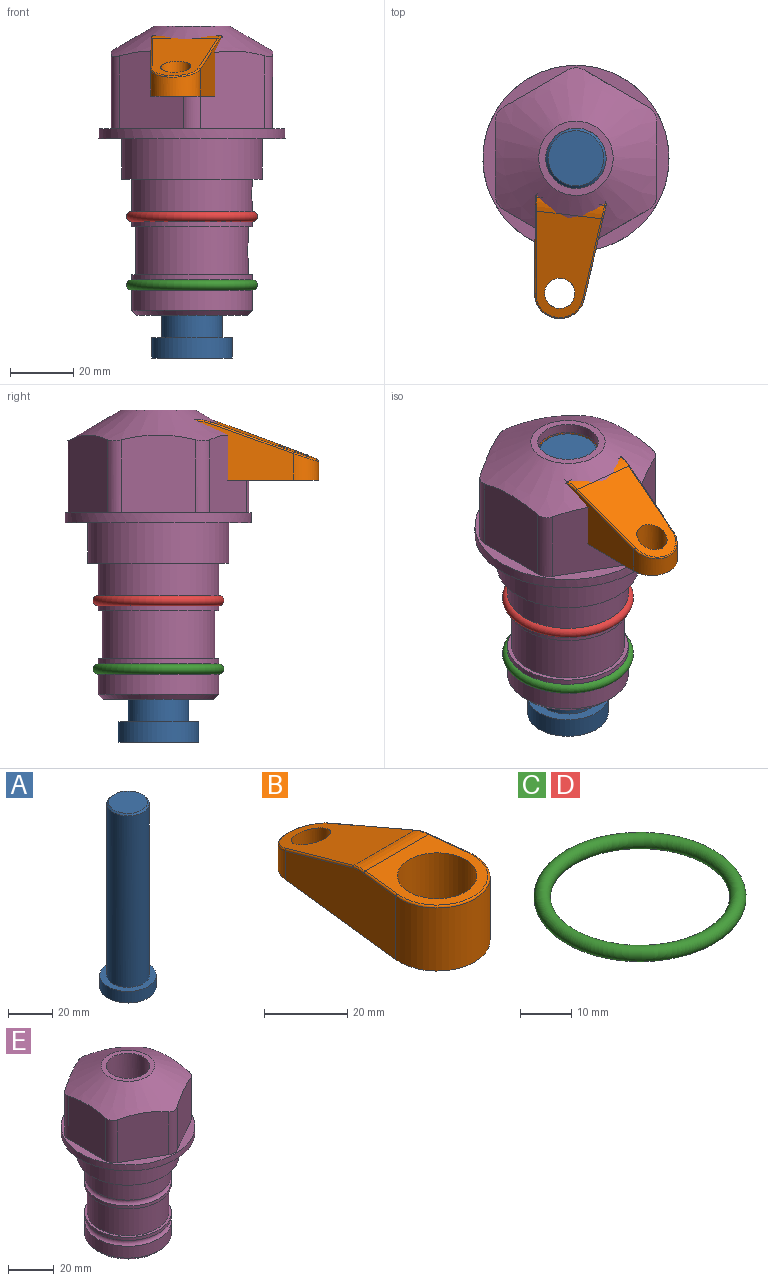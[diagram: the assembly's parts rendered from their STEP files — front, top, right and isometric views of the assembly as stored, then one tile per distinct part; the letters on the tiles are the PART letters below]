
ASSEMBLY  parts=5 mates=3
PART A: 6 faces, bbox 25.4x25.4x101.6 mm
  f0: plane 17.46x17.46mm, normal (0,0,1), area 239.5mm2, adj f5
  f1: plane 25.4x25.4mm, normal (0,0,-1), area 506.7mm2, adj f2
  f2: cylinder r=12.7mm len=25.4mm, axis (0,0,1), area 506.7mm2, adj f1,f3
  f3: plane 25.4x25.4mm, normal (0,0,1), area 221.7mm2, adj f2,f4
  f4: cylinder r=9.53mm len=94.46mm, axis (0,0,1), area 5653mm2, adj f3,f5
  f5: cone r=8.73mm half-angle=45deg, axis (0,0,-1), area 64.4mm2, adj f0,f4
PART B: 44 faces, bbox 27.5x64.5x19.1 mm
  f0: plane 2.3x0.95mm, normal (0,0,-1), area 1mm2, adj f25,f30,f34
  f1: plane 63.5x25.4mm, normal (0,0,-1), area 561.7mm2, adj f2,f3,f4,f5,f6,f7,f19,f20
  f2: cylinder r=12.7mm len=25.4mm, axis (0,0,-1), area 792.2mm2, adj f1,f3,f5,f13
  f3: plane 42.33x18.54mm, normal (0.99,0.11,0), area 647mm2, adj f1,f2,f4,f11,f12,f14
  f4: cylinder r=7.94mm len=15.78mm, axis (0,0,-1), area 158.6mm2, adj f1,f3,f5,f16
  f5: plane 42.33x18.54mm, normal (-0.99,0.11,0), area 647mm2, adj f1,f2,f4,f15,f17,f18
  f6: cylinder r=9.53mm len=19.05mm, axis (0,0,-1), area 1140.1mm2, adj f1,f8
  f7: cylinder r=4.76mm len=10.98mm, axis (0,0,-1), area 276.1mm2, adj f1,f9
  f8: plane 25.83x24.38mm, normal (0,0,1), area 262.2mm2, adj f6,f10,f11,f13,f15
  f9: plane 32.49x20.55mm, normal (0,0.34,0.94), area 489.9mm2, adj f7,f10,f14,f16,f18
  f10: cylinder r=12.7mm len=21.49mm, axis (-1,0,0), area 93.2mm2, adj f8,f9,f12,f17
  f11: cylinder r=0.51mm len=12.34mm, axis (0.11,-0.99,0), area 9.9mm2, adj f3,f8,f12,f13
  f12: bspline ~7.62x1.64mm, area 3.5mm2, adj f3,f10,f11,f14
  f13: torus R=12.19mm, axis (0,0,1), area 33.6mm2, adj f2,f8,f11,f15
  f14: cylinder r=0.51mm len=26.01mm, axis (0.1,-0.93,0.34), area 21.6mm2, adj f3,f9,f12,f16
  f15: cylinder r=0.51mm len=12.34mm, axis (0.11,0.99,0), area 9.9mm2, adj f5,f8,f13,f17
  f16: bspline ~15.78x7.05mm, area 15.7mm2, adj f4,f9,f14,f18
  f17: bspline ~7.62x1.64mm, area 3.5mm2, adj f5,f10,f15,f18
  f18: cylinder r=0.51mm len=26.01mm, axis (0.1,0.93,-0.34), area 21.6mm2, adj f5,f9,f16,f17
  f19: plane 21.6x14.29mm, normal (-0.99,-0.11,0), area 242.6mm2, adj f1,f26,f28,f34,f36,f38
  f20: plane 21.6x14.29mm, normal (0.99,-0.11,0), area 242.6mm2, adj f1,f27,f29,f37,f39,f41
  f21: cylinder r=12.7mm len=14.29mm, axis (0,0,-1), area 173.2mm2, adj f1,f26,f27,f30,f31,f33
  f22: cylinder r=7.94mm len=7.63mm, axis (0,0,-1), area 53.8mm2, adj f1,f28,f29,f42
  f23: plane 2.3x0.95mm, normal (0,0,-1), area 1mm2, adj f25,f33,f37
  f24: plane 17.94x12.32mm, normal (0,-0.34,-0.94), area 191.2mm2, adj f25,f38,f41,f42
  f25: cylinder r=9.53mm len=12.93mm, axis (-1,0,0), area 37.5mm2, adj f0,f23,f24,f31,f36,f39
  f26: cylinder r=1.59mm len=14.29mm, axis (0,0,-1), area 49mm2, adj f1,f19,f21,f32
  f27: cylinder r=1.59mm len=14.29mm, axis (0,0,-1), area 49mm2, adj f1,f20,f21,f35
  f28: cylinder r=1.59mm len=7.28mm, axis (0,0,-1), area 22.1mm2, adj f1,f19,f22,f40
  f29: cylinder r=1.59mm len=7.28mm, axis (0,0,-1), area 22.1mm2, adj f1,f20,f22,f43
  f30: torus R=14.29mm, axis (0,0,1), area 5.8mm2, adj f0,f21,f31,f32
  f31: bspline ~11.06x2.73mm, area 20.8mm2, adj f21,f25,f30,f33
  f32: sphere r=1.59mm, area 5.4mm2, adj f26,f30,f34
  f33: torus R=14.29mm, axis (0,0,1), area 5.8mm2, adj f21,f23,f31,f35
  f34: cylinder r=1.59mm len=1.68mm, axis (-0.11,0.99,0), area 2.4mm2, adj f0,f19,f32,f36
  f35: sphere r=1.59mm, area 5.4mm2, adj f27,f33,f37
  f36: bspline ~5.82x2.33mm, area 7.7mm2, adj f19,f25,f34,f38
  f37: cylinder r=1.59mm len=1.68mm, axis (0.11,0.99,0), area 2.4mm2, adj f20,f23,f35,f39
  f38: cylinder r=1.59mm len=18.33mm, axis (0.1,-0.93,0.34), area 46.7mm2, adj f19,f24,f36,f40
  f39: bspline ~5.82x2.33mm, area 7.7mm2, adj f20,f25,f37,f41
  f40: sphere r=1.59mm, area 3.6mm2, adj f28,f38,f42
  f41: cylinder r=1.59mm len=18.33mm, axis (0.1,0.93,-0.34), area 46.7mm2, adj f20,f24,f39,f43
  f42: bspline ~8.31x1.84mm, area 15.3mm2, adj f22,f24,f40,f43
  f43: sphere r=1.59mm, area 3.6mm2, adj f29,f41,f42
PART C: 1 faces, bbox 44.7x44.7x3.2 mm
  f0: torus R=19.05mm, axis (0,0,1), area 1193.9mm2
PART D: same geometry as C
PART E: 36 faces, bbox 58.7x58.7x91.2 mm
  f0: cylinder r=17.78mm len=35.56mm, axis (0,0,1), area 1670.8mm2, adj f23,f24,f31
  f1: cylinder r=19.05mm len=38.1mm, axis (0,0,1), area 1191.9mm2, adj f26,f27,f30
  f2: plane 58.66x58.66mm, normal (0,0,-1), area 1150.6mm2, adj f3,f28
  f3: cylinder r=29.33mm len=58.66mm, axis (0,0,-1), area 585.1mm2, adj f2,f4
  f4: plane 58.66x58.66mm, normal (0,0,1), area 475.9mm2, adj f3,f5,f6,f7,f8,f9,f10,f11
  f5: plane 24.5x20.32mm, normal (-0.5,0.87,0), area 562.8mm2, adj f4,f15,f16,f17
  f6: plane 24.5x20.32mm, normal (0.5,0.87,0), area 562.8mm2, adj f4,f14,f15,f17
  f7: plane 24.5x23.48mm, normal (1,0,0), area 562.8mm2, adj f4,f13,f14,f17
  f8: plane 24.5x20.32mm, normal (0.5,-0.87,0), area 562.8mm2, adj f4,f12,f13,f17
  f9: plane 24.5x20.32mm, normal (-0.5,-0.87,0), area 562.8mm2, adj f4,f11,f12,f17
  f10: plane 24.5x23.48mm, normal (-1,0,0), area 562.8mm2, adj f4,f11,f16,f17
  f11: cylinder r=5.08mm len=23.01mm, axis (0,0,-1), area 121.2mm2, adj f4,f9,f10,f17
  f12: cylinder r=5.08mm len=23.01mm, axis (0,0,-1), area 121.2mm2, adj f4,f8,f9,f17
  f13: cylinder r=5.08mm len=23.01mm, axis (0,0,-1), area 121.2mm2, adj f4,f7,f8,f17
  f14: cylinder r=5.08mm len=23.01mm, axis (0,0,-1), area 121.2mm2, adj f4,f6,f7,f17
  f15: cylinder r=5.08mm len=23.01mm, axis (0,0,-1), area 121.2mm2, adj f4,f5,f6,f17
  f16: cylinder r=5.08mm len=23.01mm, axis (0,0,-1), area 121.2mm2, adj f4,f5,f10,f17
  f17: cone r=11.73mm half-angle=60deg, axis (0,0,-1), area 2071.8mm2, adj f5,f6,f7,f8,f9,f10,f11,f12
  f18: plane 23.46x23.46mm, normal (0,0,1), area 147.4mm2, adj f17,f35
  f19: plane 34.93x34.93mm, normal (0,0,-1), area 958mm2, adj f29
  f20: cylinder r=19.05mm len=38.1mm, axis (0,0,1), area 760.1mm2, adj f21,f29
  f21: torus R=19.05mm, axis (0,0,1), area 565.3mm2, adj f20,f22
  f22: cylinder r=19.05mm len=38.1mm, axis (0,0,1), area 190mm2, adj f21,f23
  f23: plane 38.1x38.1mm, normal (0,0,1), area 146.9mm2, adj f0,f22
  f24: plane 38.1x38.1mm, normal (0,0,-1), area 146.9mm2, adj f0,f25
  f25: cylinder r=19.05mm len=38.1mm, axis (0,0,1), area 190mm2, adj f24,f26
  f26: torus R=19.05mm, axis (0,0,1), area 565.3mm2, adj f1,f25
  f27: plane 44.45x44.45mm, normal (0,0,-1), area 411.7mm2, adj f1,f28
  f28: cylinder r=22.23mm len=44.45mm, axis (0,0,1), area 1773.5mm2, adj f2,f27
  f29: cone r=19.05mm half-angle=45deg, axis (0,0,1), area 257.5mm2, adj f19,f20
  f30: cylinder r=3.17mm len=6.75mm, axis (-1,0,0), area 128mm2, adj f1,f33
  f31: cylinder r=3.17mm len=6.35mm, axis (-1,0,0), area 102.5mm2, adj f0,f33
  f32: plane 25.4x25.4mm, normal (0,0,1), area 506.7mm2, adj f33
  f33: cylinder r=12.7mm len=66.42mm, axis (0,0,-1), area 5236.2mm2, adj f30,f31,f32,f34
  f34: cone r=9.53mm half-angle=30deg, axis (0,0,-1), area 443.4mm2, adj f33,f35
  f35: cylinder r=9.53mm len=19.05mm, axis (0,0,-1), area 849mm2, adj f18,f34
PLACE A rot(axis=(0,0,-1),96.9deg) t=(0,0,-41.16)mm
PLACE B rot(axis=(0,0,1),173.1deg) t=(0,0,13.45)mm
PLACE C t=(0,0,-21.59)mm
PLACE D at identity
PLACE E at identity fixed
MATE fastened C.f0 <-> E.f0  axis (0,0,1) through (0,0,-46.1)mm
MATE cylindrical A.f2 <-> E.f0  axis (0,0,1) through (0,0,-15.53)mm
MATE fastened B.f2 <-> A.f2  axis (0,0,1) through (0,0,32.5)mm
